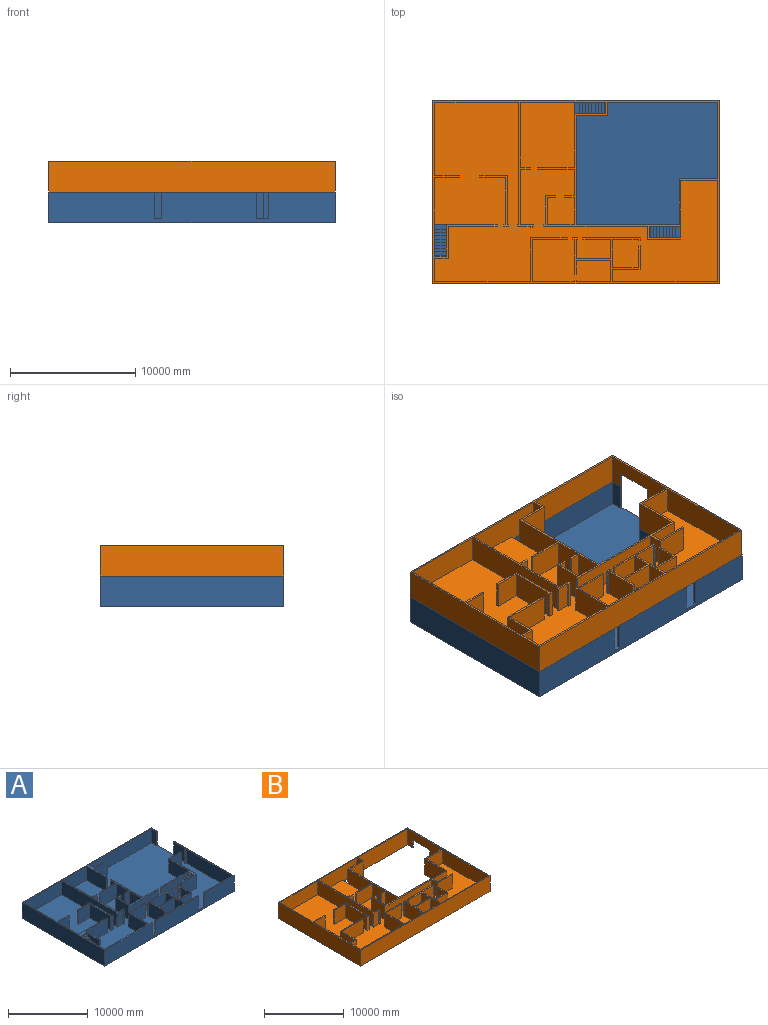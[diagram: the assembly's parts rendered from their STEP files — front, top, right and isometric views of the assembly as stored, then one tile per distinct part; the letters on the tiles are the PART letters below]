
ASSEMBLY  parts=2 mates=1
PART A: 200 faces, bbox 22860x14630.4x2438.4 mm
  f0: plane 4820.76x2133.6mm, normal (0,-1,0), area 7846867.1mm2, adj f5,f125,f133,f134,f148,f153,f154,f159
  f1: plane 2286x1920.24mm, normal (0,1,0), area 2438704.8mm2, adj f125,f134,f148,f153,f154,f159,f160,f165
  f2: plane 4165.6x2133.6mm, normal (1,0,0), area 6449019.4mm2, adj f5,f11,f53,f54,f146,f149,f150,f155
  f3: plane 11023.6x2133.6mm, normal (0,-1,0), area 21081248.2mm2, adj f5,f42,f44,f54,f147,f151,f152,f157
  f4: plane 2286x1920.24mm, normal (-1,0,0), area 2438704.8mm2, adj f11,f54,f146,f149,f150,f155,f156,f161
  f5: plane 22707.6x14478mm, normal (0,0,1), area 303124170mm2, adj f0,f2,f3,f6,f7,f11,f12,f13
  f6: plane 22860x2438.4mm, normal (0,-1,0), area 52358852mm2, adj f5,f7,f9,f10,f46,f54,f90,f91
  f7: plane 14630.4x2438.4mm, normal (1,0,0), area 29171554.6mm2, adj f5,f6,f8,f10,f45,f54,f95,f101
  f8: plane 22860x2438.4mm, normal (0,1,0), area 55741824mm2, adj f7,f9,f10,f54
  f9: plane 14630.4x2438.4mm, normal (-1,0,0), area 35674767.4mm2, adj f6,f8,f10,f54
  f10: plane 22860x14630.4mm, normal (0,0,-1), area 334450944mm2, adj f6,f7,f8,f9
  f11: plane 2133.6x1066.8mm, normal (0,-1,0), area 520257mm2, adj f2,f4,f5,f12,f54,f146
  f12: plane 2540x2133.6mm, normal (1,0,0), area 5419344mm2, adj f5,f11,f13,f54
  f13: plane 3906.1x2133.6mm, normal (0,-1,0), area 8334046.7mm2, adj f5,f12,f14,f54
  f14: plane 2133.6x152.4mm, normal (1,0,0), area 325160.6mm2, adj f5,f13,f15,f54
  f15: plane 4972.9x2133.6mm, normal (0,1,0), area 10610171.2mm2, adj f5,f14,f16,f54
  f16: plane 3715.87x2133.6mm, normal (1,0,0), area 7928179.1mm2, adj f5,f15,f17,f54
  f17: plane 2133.6x1972.95mm, normal (0,-1,0), area 4209475.9mm2, adj f5,f16,f18,f54
  f18: plane 2133.6x152.4mm, normal (1,0,0), area 325160.6mm2, adj f5,f17,f19,f54
  f19: plane 2133.6x1972.95mm, normal (0,1,0), area 4209475.9mm2, adj f5,f18,f20,f54
  f20: plane 5885.33x2133.6mm, normal (1,0,0), area 12556941.2mm2, adj f5,f19,f21,f54
  f21: plane 6705.6x2133.6mm, normal (0,-1,0), area 14307068.2mm2, adj f5,f20,f22,f54
  f22: plane 9753.6x2133.6mm, normal (-1,0,0), area 20810281mm2, adj f5,f21,f23,f54
  f23: plane 2133.6x109.6mm, normal (0,1,0), area 233834mm2, adj f5,f22,f24,f54
  f24: plane 2133.6x152.4mm, normal (-1,0,0), area 325160.6mm2, adj f5,f23,f25,f54
  f25: plane 2133.6x1024mm, normal (0,-1,0), area 2184797.8mm2, adj f5,f24,f26,f54
  f26: plane 2133.6x99.6mm, normal (-1,0,0), area 212512.3mm2, adj f5,f25,f27,f54
  f27: plane 2133.6x147.23mm, normal (0,-1,0), area 314129mm2, adj f5,f26,f28,f54
  f28: plane 2133.6x99.6mm, normal (1,0,0), area 212512.3mm2, adj f5,f27,f29,f54
  f29: plane 2133.6x131.78mm, normal (0,-1,0), area 281166.1mm2, adj f5,f28,f30,f54
  f30: plane 2133.6x152.4mm, normal (1,0,0), area 325160.6mm2, adj f5,f29,f31,f54
  f31: plane 2133.6x1041.01mm, normal (0,1,0), area 2221098.3mm2, adj f5,f30,f32,f54
  f32: plane 4419.6x2133.6mm, normal (1,0,0), area 9429658.6mm2, adj f5,f31,f33,f54
  f33: plane 2133.6x769.84mm, normal (0,-1,0), area 1642537.9mm2, adj f5,f32,f34,f54
  f34: plane 2133.6x152.4mm, normal (1,0,0), area 325160.6mm2, adj f5,f33,f35,f54
  f35: plane 2133.6x769.84mm, normal (0,1,0), area 1642537.9mm2, adj f5,f34,f36,f54
  f36: plane 5181.6x2133.6mm, normal (1,0,0), area 11055461.8mm2, adj f5,f35,f37,f54
  f37: plane 4267.2x2133.6mm, normal (0,-1,0), area 9104497.9mm2, adj f5,f36,f38,f54
  f38: plane 3466.66x2133.6mm, normal (-1,0,0), area 7396455.3mm2, adj f5,f37,f39,f54
  f39: plane 2133.6x152.4mm, normal (0,-1,0), area 325160.6mm2, adj f5,f38,f40,f54
  f40: plane 2399.86x2133.6mm, normal (1,0,0), area 5120330.8mm2, adj f5,f39,f41,f54
  f41: plane 2540x2133.6mm, normal (0,-1,0), area 5419344mm2, adj f5,f40,f42,f54
  f42: plane 2133.6x1066.8mm, normal (1,0,0), area 520257mm2, adj f3,f5,f41,f43,f54,f147
  f43: plane 2286x1920.24mm, normal (0,1,0), area 2438704.8mm2, adj f42,f54,f147,f151,f152,f157,f158,f163
  f44: plane 2133.6x914.4mm, normal (-1,0,0), area 1950963.8mm2, adj f3,f5,f45,f54
  f45: plane 2133.6x152.4mm, normal (0,-1,0), area 325160.6mm2, adj f5,f7,f44,f54
  f46: plane 2133.6x152.4mm, normal (1,0,0), area 325160.6mm2, adj f5,f6,f47,f54
  f47: plane 2133.6x523.76mm, normal (0,1,0), area 1117485.7mm2, adj f5,f46,f48,f54
  f48: plane 3352.8x2133.6mm, normal (1,0,0), area 7153534.1mm2, adj f5,f47,f49,f54
  f49: plane 2799.86x2133.6mm, normal (0,-1,0), area 5973789.3mm2, adj f5,f48,f50,f54
  f50: plane 2133.6x152.4mm, normal (1,0,0), area 325160.6mm2, adj f5,f49,f51,f54
  f51: plane 2952.26x2133.6mm, normal (0,1,0), area 6298949.9mm2, adj f5,f50,f52,f54
  f52: plane 3505.2x2133.6mm, normal (-1,0,0), area 7478694.7mm2, adj f5,f51,f53,f54
  f53: plane 7620x2133.6mm, normal (0,1,0), area 16258032mm2, adj f2,f5,f52,f54
  f54: plane 22860x14630.4mm, normal (0,0,1), area 12697478.6mm2, adj f2,f3,f4,f6,f7,f8,f9,f11
  f55: plane 2184.4x2133.6mm, normal (0,1,0), area 4660635.8mm2, adj f5,f56,f91,f92
  f56: plane 2133.6x965.5mm, normal (1,0,0), area 2060000.9mm2, adj f5,f55,f57,f92
  f57: plane 2184.4x2133.6mm, normal (0,-1,0), area 4660635.8mm2, adj f5,f56,f58,f92
  f58: plane 2133.6x1887.35mm, normal (1,0,0), area 4026843.9mm2, adj f5,f57,f59,f92
  f59: plane 2133.6x152.4mm, normal (0,1,0), area 325160.6mm2, adj f5,f58,f60,f92
  f60: plane 2133.6x1734.95mm, normal (-1,0,0), area 3701683.3mm2, adj f5,f59,f61,f92
  f61: plane 2133.6x2032mm, normal (0,1,0), area 4335475.2mm2, adj f5,f60,f62,f92
  f62: plane 2234.9x2133.6mm, normal (1,0,0), area 4768372.6mm2, adj f5,f61,f63,f92
  f63: plane 2133.6x2032mm, normal (0,-1,0), area 4335475.2mm2, adj f5,f62,f64,f92
  f64: plane 2133.6x88.36mm, normal (-1,0,0), area 188515.1mm2, adj f5,f63,f65,f92
  f65: plane 2133.6x152.4mm, normal (0,-1,0), area 325160.6mm2, adj f5,f64,f66,f92
  f66: plane 2133.6x88.36mm, normal (1,0,0), area 188515.1mm2, adj f5,f65,f67,f92
  f67: plane 2133.6x78.39mm, normal (0,-1,0), area 167258.4mm2, adj f5,f66,f68,f92
  f68: plane 2133.6x152.4mm, normal (1,0,0), area 325160.6mm2, adj f5,f67,f69,f92
  f69: plane 4633.07x2133.6mm, normal (0,1,0), area 9885118.1mm2, adj f5,f68,f70,f92
  f70: plane 2133.6x152.4mm, normal (-1,0,0), area 325160.6mm2, adj f5,f69,f71,f92
  f71: plane 2217.88x2133.6mm, normal (0,-1,0), area 4732063.2mm2, adj f5,f70,f72,f92
  f72: plane 2133.6x1524mm, normal (-1,0,0), area 3251606.4mm2, adj f5,f71,f73,f92
  f73: plane 2773.87x2133.6mm, normal (0,1,0), area 5918320.5mm2, adj f5,f72,f74,f92
  f74: plane 2133.6x1524mm, normal (1,0,0), area 3251606.4mm2, adj f5,f73,f75,f92
  f75: plane 2133.6x141.82mm, normal (0,-1,0), area 302591.8mm2, adj f5,f74,f76,f92
  f76: plane 2133.6x152.4mm, normal (1,0,0), area 325160.6mm2, adj f5,f75,f77,f92
  f77: plane 2133.6x404.75mm, normal (0,1,0), area 863582.5mm2, adj f5,f76,f78,f92
  f78: plane 2133.6x152.4mm, normal (-1,0,0), area 325160.6mm2, adj f5,f77,f79,f92
  f79: plane 2133.6x110.53mm, normal (0,-1,0), area 235830mm2, adj f5,f78,f80,f92
  f80: plane 2775.92x2133.6mm, normal (-1,0,0), area 5922708.9mm2, adj f5,f79,f81,f92
  f81: plane 2133.6x152.4mm, normal (0,-1,0), area 325160.6mm2, adj f5,f80,f82,f92
  f82: plane 2133.6x1099.52mm, normal (1,0,0), area 2345941.9mm2, adj f5,f81,f83,f92
  f83: plane 2773.87x2133.6mm, normal (0,-1,0), area 5918320.5mm2, adj f5,f82,f84,f92
  f84: plane 2133.6x1676.4mm, normal (-1,0,0), area 3576767mm2, adj f5,f83,f85,f92
  f85: plane 2773.87x2133.6mm, normal (0,1,0), area 5918320.5mm2, adj f5,f84,f86,f92
  f86: plane 2133.6x124.28mm, normal (1,0,0), area 265155mm2, adj f5,f85,f87,f92
  f87: plane 2133.6x152.4mm, normal (0,1,0), area 325160.6mm2, adj f5,f86,f88,f92
  f88: plane 2133.6x124.28mm, normal (-1,0,0), area 265155mm2, adj f5,f87,f89,f92
  f89: plane 2269.95x2133.6mm, normal (0,1,0), area 4843162.5mm2, adj f5,f88,f90,f92
  f90: plane 2133.6x152.4mm, normal (-1,0,0), area 325160.6mm2, adj f5,f6,f89,f92
  f91: plane 2133.6x152.4mm, normal (1,0,0), area 325160.6mm2, adj f5,f6,f55,f92
  f92: plane 7611.41x3657.6mm, normal (0,0,1), area 3902263.8mm2, adj f6,f55,f56,f57,f58,f59,f60,f61
  f93: plane 5140.46x2133.6mm, normal (0,1,0), area 10967684.2mm2, adj f5,f94,f100,f101
  f94: plane 2133.6x152.4mm, normal (-1,0,0), area 325160.6mm2, adj f5,f6,f93,f101
  f95: plane 2133.6x152.4mm, normal (0,1,0), area 325160.6mm2, adj f5,f7,f96,f101
  f96: plane 2133.6x2133.6mm, normal (-1,0,0), area 4552249mm2, adj f5,f95,f97,f101
  f97: plane 2133.6x208.14mm, normal (0,1,0), area 444091.1mm2, adj f5,f96,f98,f101
  f98: plane 2133.6x152.4mm, normal (-1,0,0), area 325160.6mm2, adj f5,f97,f99,f101
  f99: plane 2133.6x208.14mm, normal (0,-1,0), area 444091.1mm2, adj f5,f98,f100,f101
  f100: plane 8077.2x2133.6mm, normal (-1,0,0), area 17233513.9mm2, adj f5,f93,f99,f101
  f101: plane 10515.6x5292.86mm, normal (0,0,1), area 2417704.2mm2, adj f6,f7,f93,f94,f95,f96,f97,f98
  f102: plane 2133.6x820.02mm, normal (0,1,0), area 1749586mm2, adj f5,f103,f123,f124
  f103: plane 2286x2133.6mm, normal (-1,0,0), area 4877409.6mm2, adj f5,f102,f104,f124
  f104: plane 2133.6x130.68mm, normal (0,1,0), area 278827.1mm2, adj f5,f103,f105,f124
  f105: plane 2133.6x152.4mm, normal (-1,0,0), area 325160.6mm2, adj f5,f104,f106,f124
  f106: plane 5177.77x2133.6mm, normal (0,-1,0), area 11047297.5mm2, adj f5,f105,f107,f124
  f107: plane 2133.6x152.4mm, normal (1,0,0), area 325160.6mm2, adj f5,f106,f108,f124
  f108: plane 2608.69x2133.6mm, normal (0,1,0), area 5565900.2mm2, adj f5,f107,f109,f124
  f109: plane 5514.86x2133.6mm, normal (1,0,0), area 11766504.7mm2, adj f5,f108,f110,f124
  f110: plane 2133.6x152.4mm, normal (0,1,0), area 325160.6mm2, adj f5,f109,f111,f124
  f111: plane 2133.6x942.86mm, normal (-1,0,0), area 2011685.5mm2, adj f5,f110,f112,f124
  f112: plane 2916.77x2133.6mm, normal (0,1,0), area 6223219.8mm2, adj f5,f111,f113,f124
  f113: plane 2133.6x152.4mm, normal (-1,0,0), area 325160.6mm2, adj f5,f112,f114,f124
  f114: plane 2916.77x2133.6mm, normal (0,-1,0), area 6223219.8mm2, adj f5,f113,f115,f124
  f115: plane 2133.6x2133.6mm, normal (-1,0,0), area 4552249mm2, adj f5,f114,f116,f124
  f116: plane 2133.6x769.43mm, normal (0,1,0), area 1641659.6mm2, adj f5,f115,f117,f124
  f117: plane 2133.6x152.4mm, normal (-1,0,0), area 325160.6mm2, adj f5,f116,f118,f124
  f118: plane 2133.6x769.43mm, normal (0,-1,0), area 1641659.6mm2, adj f5,f117,f119,f124
  f119: plane 2133.6x2133.6mm, normal (-1,0,0), area 4552249mm2, adj f5,f118,f120,f124
  f120: plane 2133.6x2133.6mm, normal (0,1,0), area 4552249mm2, adj f5,f119,f121,f124
  f121: plane 2133.6x2133.6mm, normal (1,0,0), area 4552249mm2, adj f5,f120,f122,f124
  f122: plane 2133.6x667.62mm, normal (0,-1,0), area 1424425.4mm2, adj f5,f121,f123,f124
  f123: plane 2133.6x152.4mm, normal (1,0,0), area 325160.6mm2, adj f5,f102,f122,f124
  f124: plane 5677.86x5667.26mm, normal (0,0,1), area 2641465.5mm2, adj f102,f103,f104,f105,f106,f107,f108,f109
  f125: plane 2133.6x1066.8mm, normal (-1,0,0), area 520257mm2, adj f0,f1,f5,f126,f134,f148
  f126: plane 2692.4x2133.6mm, normal (0,-1,0), area 5744504.6mm2, adj f5,f125,f127,f134
  f127: plane 4724.4x2133.6mm, normal (1,0,0), area 10079979.8mm2, adj f5,f126,f128,f134
  f128: plane 2133.6x1993.44mm, normal (0,-1,0), area 4253205.5mm2, adj f5,f127,f129,f134
  f129: plane 2133.6x152.4mm, normal (1,0,0), area 325160.6mm2, adj f5,f128,f130,f134
  f130: plane 2145.84x2133.6mm, normal (0,1,0), area 4578366.2mm2, adj f5,f129,f131,f134
  f131: plane 3657.6x2133.6mm, normal (-1,0,0), area 7803855.4mm2, adj f5,f130,f132,f134
  f132: plane 5074.76x2133.6mm, normal (0,1,0), area 10827506.3mm2, adj f5,f131,f133,f134
  f133: plane 2133.6x152.4mm, normal (-1,0,0), area 325160.6mm2, adj f0,f5,f132,f134
  f134: plane 7220.6x4876.8mm, normal (0,0,1), area 2439771.6mm2, adj f0,f1,f125,f126,f127,f128,f129,f130
  f135: plane 2133.6x128.6mm, normal (0,1,0), area 274378.8mm2, adj f5,f136,f144,f145
  f136: plane 2133.6x152.4mm, normal (-1,0,0), area 325160.6mm2, adj f5,f135,f137,f145
  f137: plane 2133.6x380.59mm, normal (0,-1,0), area 812028.8mm2, adj f5,f136,f138,f145
  f138: plane 2133.6x152.4mm, normal (1,0,0), area 325160.6mm2, adj f5,f137,f139,f145
  f139: plane 2133.6x99.59mm, normal (0,1,0), area 212489.3mm2, adj f5,f138,f140,f145
  f140: plane 3868.27x2133.6mm, normal (1,0,0), area 8253339.8mm2, adj f5,f139,f141,f145
  f141: plane 2183.95x2133.6mm, normal (0,1,0), area 4659682.3mm2, adj f5,f140,f142,f145
  f142: plane 2133.6x152.4mm, normal (-1,0,0), area 325160.6mm2, adj f5,f141,f143,f145
  f143: plane 2133.6x2031.55mm, normal (0,-1,0), area 4334521.7mm2, adj f5,f142,f144,f145
  f144: plane 3715.87x2133.6mm, normal (-1,0,0), area 7928179.1mm2, adj f5,f135,f143,f145
  f145: plane 4020.67x2283.55mm, normal (0,0,1), area 957135mm2, adj f135,f136,f137,f138,f139,f140,f141,f142
  f146: plane 914.4x254mm, normal (0,0,1), area 232257.6mm2, adj f2,f4,f11,f149
  f147: plane 914.4x254mm, normal (0,0,1), area 232257.6mm2, adj f3,f42,f43,f151
  f148: plane 914.4x254mm, normal (0,0,1), area 232257.6mm2, adj f0,f1,f125,f153
  f149: plane 914.4x213.36mm, normal (0,-1,0), area 195096.4mm2, adj f2,f4,f146,f150
  f150: plane 914.4x254mm, normal (0,0,1), area 232257.6mm2, adj f2,f4,f149,f155
  f151: plane 914.4x213.36mm, normal (1,0,0), area 195096.4mm2, adj f3,f43,f147,f152
  f152: plane 914.4x254mm, normal (0,0,1), area 232257.6mm2, adj f3,f43,f151,f157
  f153: plane 914.4x213.36mm, normal (-1,0,0), area 195096.4mm2, adj f0,f1,f148,f154
  f154: plane 914.4x254mm, normal (0,0,1), area 232257.6mm2, adj f0,f1,f153,f159
  f155: plane 914.4x213.36mm, normal (0,-1,0), area 195096.4mm2, adj f2,f4,f150,f156
  f156: plane 914.4x254mm, normal (0,0,1), area 232257.6mm2, adj f2,f4,f155,f161
  f157: plane 914.4x213.36mm, normal (1,0,0), area 195096.4mm2, adj f3,f43,f152,f158
  f158: plane 914.4x254mm, normal (0,0,1), area 232257.6mm2, adj f3,f43,f157,f163
  f159: plane 914.4x213.36mm, normal (-1,0,0), area 195096.4mm2, adj f0,f1,f154,f160
  f160: plane 914.4x254mm, normal (0,0,1), area 232257.6mm2, adj f0,f1,f159,f165
  f161: plane 914.4x213.36mm, normal (0,-1,0), area 195096.4mm2, adj f2,f4,f156,f162
  f162: plane 914.4x254mm, normal (0,0,1), area 232257.6mm2, adj f2,f4,f161,f167
  f163: plane 914.4x213.36mm, normal (1,0,0), area 195096.4mm2, adj f3,f43,f158,f164
  f164: plane 914.4x254mm, normal (0,0,1), area 232257.6mm2, adj f3,f43,f163,f169
  f165: plane 914.4x213.36mm, normal (-1,0,0), area 195096.4mm2, adj f0,f1,f160,f166
  f166: plane 914.4x254mm, normal (0,0,1), area 232257.6mm2, adj f0,f1,f165,f171
  f167: plane 914.4x213.36mm, normal (0,-1,0), area 195096.4mm2, adj f2,f4,f162,f168
  f168: plane 914.4x254mm, normal (0,0,1), area 232257.6mm2, adj f2,f4,f167,f173
  f169: plane 914.4x213.36mm, normal (1,0,0), area 195096.4mm2, adj f3,f43,f164,f170
  f170: plane 914.4x254mm, normal (0,0,1), area 232257.6mm2, adj f3,f43,f169,f175
  f171: plane 914.4x213.36mm, normal (-1,0,0), area 195096.4mm2, adj f0,f1,f166,f172
  f172: plane 914.4x254mm, normal (0,0,1), area 232257.6mm2, adj f0,f1,f171,f177
  f173: plane 914.4x213.36mm, normal (0,-1,0), area 195096.4mm2, adj f2,f4,f168,f174
  f174: plane 914.4x254mm, normal (0,0,1), area 232257.6mm2, adj f2,f4,f173,f179
  f175: plane 914.4x213.36mm, normal (1,0,0), area 195096.4mm2, adj f3,f43,f170,f176
  f176: plane 914.4x254mm, normal (0,0,1), area 232257.6mm2, adj f3,f43,f175,f181
  f177: plane 914.4x213.36mm, normal (-1,0,0), area 195096.4mm2, adj f0,f1,f172,f178
  f178: plane 914.4x254mm, normal (0,0,1), area 232257.6mm2, adj f0,f1,f177,f183
  f179: plane 914.4x213.36mm, normal (0,-1,0), area 195096.4mm2, adj f2,f4,f174,f180
  f180: plane 914.4x254mm, normal (0,0,1), area 232257.6mm2, adj f2,f4,f179,f185
  f181: plane 914.4x213.36mm, normal (1,0,0), area 195096.4mm2, adj f3,f43,f176,f182
  f182: plane 914.4x254mm, normal (0,0,1), area 232257.6mm2, adj f3,f43,f181,f187
  f183: plane 914.4x213.36mm, normal (-1,0,0), area 195096.4mm2, adj f0,f1,f178,f184
  f184: plane 914.4x254mm, normal (0,0,1), area 232257.6mm2, adj f0,f1,f183,f189
  f185: plane 914.4x213.36mm, normal (0,-1,0), area 195096.4mm2, adj f2,f4,f180,f186
  f186: plane 914.4x254mm, normal (0,0,1), area 232257.6mm2, adj f2,f4,f185,f191
  f187: plane 914.4x213.36mm, normal (1,0,0), area 195096.4mm2, adj f3,f43,f182,f188
  f188: plane 914.4x254mm, normal (0,0,1), area 232257.6mm2, adj f3,f43,f187,f195
  f189: plane 914.4x213.36mm, normal (-1,0,0), area 195096.4mm2, adj f0,f1,f184,f190
  f190: plane 914.4x254mm, normal (0,0,1), area 232257.6mm2, adj f0,f1,f189,f193
  f191: plane 914.4x213.36mm, normal (0,-1,0), area 195096.4mm2, adj f2,f4,f186,f192
  f192: plane 914.4x254mm, normal (0,0,1), area 232257.6mm2, adj f2,f4,f191,f198
  f193: plane 914.4x213.36mm, normal (-1,0,0), area 195096.4mm2, adj f0,f1,f190,f194
  f194: plane 914.4x254mm, normal (0,0,1), area 232257.6mm2, adj f0,f1,f193,f199
  f195: plane 914.4x213.36mm, normal (1,0,0), area 195096.4mm2, adj f3,f43,f188,f196
  f196: plane 914.4x254mm, normal (0,0,1), area 232257.6mm2, adj f3,f43,f195,f197
  f197: plane 914.4x213.36mm, normal (1,0,0), area 195096.4mm2, adj f3,f43,f54,f196
  f198: plane 914.4x213.36mm, normal (0,-1,0), area 195096.4mm2, adj f2,f4,f54,f192
  f199: plane 914.4x213.36mm, normal (-1,0,0), area 195096.4mm2, adj f0,f1,f134,f194
PART B: 132 faces, bbox 22860x14630.4x2438.4 mm
  f0: plane 22860x14630.4mm, normal (0,0,-1), area 230879538.2mm2, adj f1,f3,f4,f5,f6,f7,f8,f9
  f1: plane 14630.4x2438.4mm, normal (1,0,0), area 31958645.8mm2, adj f0,f11,f21,f117,f129,f130,f131
  f2: plane 22555.2x14325.6mm, normal (0,0,1), area 205972183.9mm2, adj f12,f15,f16,f18,f22,f26,f27,f28
  f3: plane 3657.6x2438.4mm, normal (-1,0,0), area 8918691.8mm2, adj f0,f4,f25,f117
  f4: plane 8229.6x2438.4mm, normal (0,1,0), area 20067056.6mm2, adj f0,f3,f5,f117
  f5: plane 8686.8x2438.4mm, normal (1,0,0), area 21181893.1mm2, adj f0,f4,f6,f117
  f6: plane 2540x2438.4mm, normal (0,-1,0), area 6193536mm2, adj f0,f5,f7,f117
  f7: plane 2438.4x1066.8mm, normal (1,0,0), area 2601285.1mm2, adj f0,f6,f8,f117
  f8: plane 8737.6x2438.4mm, normal (0,-1,0), area 21305763.8mm2, adj f0,f7,f9,f117
  f9: plane 6096x2438.4mm, normal (-1,0,0), area 11148364.8mm2, adj f0,f8,f25,f117,f129,f130,f131
  f10: plane 14630.4x2438.4mm, normal (-1,0,0), area 35674767.4mm2, adj f0,f11,f21,f117
  f11: plane 22860x2438.4mm, normal (0,-1,0), area 55741824mm2, adj f0,f1,f10,f117
  f12: plane 914.4x304.8mm, normal (0,-1,0), area 278709.1mm2, adj f0,f2,f13,f22
  f13: plane 2540x2438.4mm, normal (-1,0,0), area 6193536mm2, adj f0,f12,f14,f39,f117
  f14: plane 2438.4x914.4mm, normal (0,1,0), area 2229673mm2, adj f0,f13,f22,f117
  f15: plane 914.4x304.8mm, normal (1,0,0), area 278709.1mm2, adj f0,f2,f16,f23
  f16: plane 6807.2x2438.4mm, normal (0,-1,0), area 15298033.9mm2, adj f0,f2,f15,f17,f59,f117
  f17: plane 2438.4x914.4mm, normal (-1,0,0), area 2229673mm2, adj f0,f16,f23,f117
  f18: plane 914.4x304.8mm, normal (-1,0,0), area 278709.1mm2, adj f0,f2,f19,f24
  f19: plane 2540x2438.4mm, normal (0,1,0), area 6193536mm2, adj f0,f18,f20,f80,f117
  f20: plane 2438.4x914.4mm, normal (1,0,0), area 2229673mm2, adj f0,f19,f24,f117
  f21: plane 22860x2438.4mm, normal (0,1,0), area 55741824mm2, adj f0,f1,f10,f117
  f22: plane 6255.87x2438.4mm, normal (1,0,0), area 14121715.1mm2, adj f0,f2,f12,f14,f40,f117
  f23: plane 2540x2438.4mm, normal (0,1,0), area 6193536mm2, adj f0,f15,f17,f60,f117
  f24: plane 2540x2438.4mm, normal (0,-1,0), area 6193536mm2, adj f0,f18,f20,f81,f117
  f25: plane 3048x2438.4mm, normal (0,1,0), area 7432243.2mm2, adj f0,f3,f9,f117
  f26: plane 2133.6x124.28mm, normal (-1,0,0), area 265155mm2, adj f2,f27,f116,f117
  f27: plane 3352.8x2133.6mm, normal (0,1,0), area 7153534.1mm2, adj f2,f26,f28,f117
  f28: plane 3352.8x2133.6mm, normal (1,0,0), area 7153534.1mm2, adj f2,f27,f29,f117
  f29: plane 2799.86x2133.6mm, normal (0,-1,0), area 5973789.3mm2, adj f2,f28,f30,f117
  f30: plane 2133.6x152.4mm, normal (1,0,0), area 325160.6mm2, adj f2,f29,f31,f117
  f31: plane 2952.26x2133.6mm, normal (0,1,0), area 6298949.9mm2, adj f2,f30,f32,f117
  f32: plane 3505.2x2133.6mm, normal (-1,0,0), area 7478694.7mm2, adj f2,f31,f33,f117
  f33: plane 7620x2133.6mm, normal (0,1,0), area 16258032mm2, adj f2,f32,f34,f117
  f34: plane 2133.6x1879.6mm, normal (1,0,0), area 4010314.6mm2, adj f2,f33,f35,f117
  f35: plane 2133.6x1066.8mm, normal (0,-1,0), area 2276124.5mm2, adj f2,f34,f36,f117
  f36: plane 2540x2133.6mm, normal (1,0,0), area 5419344mm2, adj f2,f35,f37,f117
  f37: plane 3906.1x2133.6mm, normal (0,-1,0), area 8334046.7mm2, adj f2,f36,f38,f117
  f38: plane 2133.6x152.4mm, normal (1,0,0), area 325160.6mm2, adj f2,f37,f39,f117
  f39: plane 4058.5x2133.6mm, normal (0,1,0), area 8659207.3mm2, adj f2,f13,f38,f117
  f40: plane 2133.6x1972.95mm, normal (0,-1,0), area 4209475.9mm2, adj f2,f22,f41,f117
  f41: plane 2133.6x152.4mm, normal (1,0,0), area 325160.6mm2, adj f2,f40,f42,f117
  f42: plane 2133.6x1972.95mm, normal (0,1,0), area 4209475.9mm2, adj f2,f41,f43,f117
  f43: plane 5885.33x2133.6mm, normal (1,0,0), area 12556941.2mm2, adj f2,f42,f44,f117
  f44: plane 6705.6x2133.6mm, normal (0,-1,0), area 14307068.2mm2, adj f2,f43,f45,f117
  f45: plane 9753.6x2133.6mm, normal (-1,0,0), area 20810281mm2, adj f2,f44,f46,f117
  f46: plane 2133.6x109.6mm, normal (0,1,0), area 233834mm2, adj f2,f45,f47,f117
  f47: plane 2133.6x152.4mm, normal (-1,0,0), area 325160.6mm2, adj f2,f46,f48,f117
  f48: plane 2133.6x1024mm, normal (0,-1,0), area 2184797.8mm2, adj f2,f47,f49,f117
  f49: plane 2133.6x99.6mm, normal (-1,0,0), area 212512.3mm2, adj f2,f48,f50,f117
  f50: plane 2133.6x147.23mm, normal (0,-1,0), area 314129mm2, adj f2,f49,f51,f117
  f51: plane 2133.6x99.6mm, normal (1,0,0), area 212512.3mm2, adj f2,f50,f52,f117
  f52: plane 2133.6x131.78mm, normal (0,-1,0), area 281166.1mm2, adj f2,f51,f53,f117
  f53: plane 2133.6x152.4mm, normal (1,0,0), area 325160.6mm2, adj f2,f52,f54,f117
  f54: plane 2133.6x1041.01mm, normal (0,1,0), area 2221098.3mm2, adj f2,f53,f55,f117
  f55: plane 4419.6x2133.6mm, normal (1,0,0), area 9429658.6mm2, adj f2,f54,f56,f117
  f56: plane 2133.6x769.84mm, normal (0,-1,0), area 1642537.9mm2, adj f2,f55,f57,f117
  f57: plane 2133.6x152.4mm, normal (1,0,0), area 325160.6mm2, adj f2,f56,f58,f117
  f58: plane 2133.6x769.84mm, normal (0,1,0), area 1642537.9mm2, adj f2,f57,f59,f117
  f59: plane 5181.6x2133.6mm, normal (1,0,0), area 11055461.8mm2, adj f2,f16,f58,f117
  f60: plane 4267.2x2133.6mm, normal (-1,0,0), area 9104497.9mm2, adj f2,f23,f61,f117
  f61: plane 2916.77x2133.6mm, normal (0,1,0), area 6223219.8mm2, adj f2,f60,f62,f117
  f62: plane 2133.6x152.4mm, normal (-1,0,0), area 325160.6mm2, adj f2,f61,f63,f117
  f63: plane 2916.77x2133.6mm, normal (0,-1,0), area 6223219.8mm2, adj f2,f62,f64,f117
  f64: plane 2133.6x2133.6mm, normal (-1,0,0), area 4552249mm2, adj f2,f63,f65,f117
  f65: plane 2133.6x769.43mm, normal (0,1,0), area 1641659.6mm2, adj f2,f64,f66,f117
  f66: plane 2133.6x152.4mm, normal (-1,0,0), area 325160.6mm2, adj f2,f65,f67,f117
  f67: plane 2133.6x769.43mm, normal (0,-1,0), area 1641659.6mm2, adj f2,f66,f68,f117
  f68: plane 2133.6x2133.6mm, normal (-1,0,0), area 4552249mm2, adj f2,f67,f69,f117
  f69: plane 2133.6x2133.6mm, normal (0,1,0), area 4552249mm2, adj f2,f68,f70,f117
  f70: plane 2133.6x2133.6mm, normal (1,0,0), area 4552249mm2, adj f2,f69,f71,f117
  f71: plane 2133.6x667.62mm, normal (0,-1,0), area 1424425.4mm2, adj f2,f70,f72,f117
  f72: plane 2133.6x152.4mm, normal (1,0,0), area 325160.6mm2, adj f2,f71,f73,f117
  f73: plane 2133.6x820.02mm, normal (0,1,0), area 1749586mm2, adj f2,f72,f74,f117
  f74: plane 2286x2133.6mm, normal (-1,0,0), area 4877409.6mm2, adj f2,f73,f75,f117
  f75: plane 2133.6x130.68mm, normal (0,1,0), area 278827.1mm2, adj f2,f74,f76,f117
  f76: plane 2133.6x152.4mm, normal (-1,0,0), area 325160.6mm2, adj f2,f75,f77,f117
  f77: plane 8258.68x2133.6mm, normal (0,-1,0), area 17620727.9mm2, adj f2,f76,f78,f117
  f78: plane 2133.6x1066.8mm, normal (-1,0,0), area 2276124.5mm2, adj f2,f77,f79,f117
  f79: plane 2692.4x2133.6mm, normal (0,-1,0), area 5744504.6mm2, adj f2,f78,f80,f117
  f80: plane 2133.6x152.4mm, normal (1,0,0), area 325160.6mm2, adj f2,f19,f79,f117
  f81: plane 3657.6x2133.6mm, normal (1,0,0), area 7803855.4mm2, adj f2,f24,f82,f117
  f82: plane 2895.6x2133.6mm, normal (0,-1,0), area 6178052.2mm2, adj f2,f81,f83,f117
  f83: plane 8077.2x2133.6mm, normal (-1,0,0), area 17233513.9mm2, adj f2,f82,f84,f117
  f84: plane 8351.33x2133.6mm, normal (0,1,0), area 17818406.2mm2, adj f2,f83,f85,f117
  f85: plane 2133.6x965.5mm, normal (1,0,0), area 2060000.9mm2, adj f2,f84,f86,f117
  f86: plane 2184.4x2133.6mm, normal (0,-1,0), area 4660635.8mm2, adj f2,f85,f87,f117
  f87: plane 2133.6x1887.35mm, normal (1,0,0), area 4026843.9mm2, adj f2,f86,f88,f117
  f88: plane 2133.6x152.4mm, normal (0,1,0), area 325160.6mm2, adj f2,f87,f89,f117
  f89: plane 2133.6x1734.95mm, normal (-1,0,0), area 3701683.3mm2, adj f2,f88,f90,f117
  f90: plane 2133.6x2032mm, normal (0,1,0), area 4335475.2mm2, adj f2,f89,f91,f117
  f91: plane 2234.9x2133.6mm, normal (1,0,0), area 4768372.6mm2, adj f2,f90,f92,f117
  f92: plane 2133.6x2032mm, normal (0,-1,0), area 4335475.2mm2, adj f2,f91,f93,f117
  f93: plane 2133.6x88.36mm, normal (-1,0,0), area 188515.1mm2, adj f2,f92,f94,f117
  f94: plane 2133.6x152.4mm, normal (0,-1,0), area 325160.6mm2, adj f2,f93,f95,f117
  f95: plane 2133.6x88.36mm, normal (1,0,0), area 188515.1mm2, adj f2,f94,f96,f117
  f96: plane 2133.6x78.39mm, normal (0,-1,0), area 167258.4mm2, adj f2,f95,f97,f117
  f97: plane 2133.6x152.4mm, normal (1,0,0), area 325160.6mm2, adj f2,f96,f98,f117
  f98: plane 4633.07x2133.6mm, normal (0,1,0), area 9885118.1mm2, adj f2,f97,f99,f117
  f99: plane 2133.6x152.4mm, normal (-1,0,0), area 325160.6mm2, adj f2,f98,f100,f117
  f100: plane 2217.88x2133.6mm, normal (0,-1,0), area 4732063.2mm2, adj f2,f99,f101,f117
  f101: plane 2133.6x1524mm, normal (-1,0,0), area 3251606.4mm2, adj f2,f100,f102,f117
  f102: plane 2773.87x2133.6mm, normal (0,1,0), area 5918320.5mm2, adj f2,f101,f103,f117
  f103: plane 2133.6x1524mm, normal (1,0,0), area 3251606.4mm2, adj f2,f102,f104,f117
  f104: plane 2133.6x141.82mm, normal (0,-1,0), area 302591.8mm2, adj f2,f103,f105,f117
  f105: plane 2133.6x152.4mm, normal (1,0,0), area 325160.6mm2, adj f2,f104,f106,f117
  f106: plane 2133.6x404.75mm, normal (0,1,0), area 863582.5mm2, adj f2,f105,f107,f117
  f107: plane 2133.6x152.4mm, normal (-1,0,0), area 325160.6mm2, adj f2,f106,f108,f117
  f108: plane 2133.6x110.53mm, normal (0,-1,0), area 235830mm2, adj f2,f107,f109,f117
  f109: plane 2775.92x2133.6mm, normal (-1,0,0), area 5922708.9mm2, adj f2,f108,f110,f117
  f110: plane 2133.6x152.4mm, normal (0,-1,0), area 325160.6mm2, adj f2,f109,f111,f117
  f111: plane 2133.6x1099.52mm, normal (1,0,0), area 2345941.9mm2, adj f2,f110,f112,f117
  f112: plane 2773.87x2133.6mm, normal (0,-1,0), area 5918320.5mm2, adj f2,f111,f113,f117
  f113: plane 2133.6x1676.4mm, normal (-1,0,0), area 3576767mm2, adj f2,f112,f114,f117
  f114: plane 2773.87x2133.6mm, normal (0,1,0), area 5918320.5mm2, adj f2,f113,f115,f117
  f115: plane 2133.6x124.28mm, normal (1,0,0), area 265155mm2, adj f2,f114,f116,f117
  f116: plane 2133.6x152.4mm, normal (0,1,0), area 325160.6mm2, adj f2,f26,f115,f117
  f117: plane 22860x14630.4mm, normal (0,0,1), area 24414734.5mm2, adj f1,f3,f4,f5,f6,f7,f8,f9
  f118: plane 2133.6x128.6mm, normal (0,1,0), area 274378.8mm2, adj f2,f119,f127,f128
  f119: plane 2133.6x152.4mm, normal (-1,0,0), area 325160.6mm2, adj f2,f118,f120,f128
  f120: plane 2133.6x380.59mm, normal (0,-1,0), area 812028.8mm2, adj f2,f119,f121,f128
  f121: plane 2133.6x152.4mm, normal (1,0,0), area 325160.6mm2, adj f2,f120,f122,f128
  f122: plane 2133.6x99.59mm, normal (0,1,0), area 212489.3mm2, adj f2,f121,f123,f128
  f123: plane 3868.27x2133.6mm, normal (1,0,0), area 8253339.8mm2, adj f2,f122,f124,f128
  f124: plane 2183.95x2133.6mm, normal (0,1,0), area 4659682.3mm2, adj f2,f123,f125,f128
  f125: plane 2133.6x152.4mm, normal (-1,0,0), area 325160.6mm2, adj f2,f124,f126,f128
  f126: plane 2133.6x2031.55mm, normal (0,-1,0), area 4334521.7mm2, adj f2,f125,f127,f128
  f127: plane 3715.87x2133.6mm, normal (-1,0,0), area 7928179.1mm2, adj f2,f118,f126,f128
  f128: plane 4020.67x2283.55mm, normal (0,0,1), area 957135mm2, adj f118,f119,f120,f121,f122,f123,f124,f125
  f129: plane 1219.2x152.4mm, normal (0,1,0), area 185806.1mm2, adj f0,f1,f9,f131
  f130: plane 1219.2x152.4mm, normal (0,-1,0), area 185806.1mm2, adj f0,f1,f9,f131
  f131: plane 3048x152.4mm, normal (0,0,-1), area 464515.2mm2, adj f1,f9,f129,f130
PLACE A t=(-775.89,-231.34,484.66)mm fixed
PLACE B t=(-775.89,18016.67,2923.06)mm
MATE fastened A.f101 <-> B.f0  axis (0,0,1) through (22084.11,-231.34,2618.26)mm
